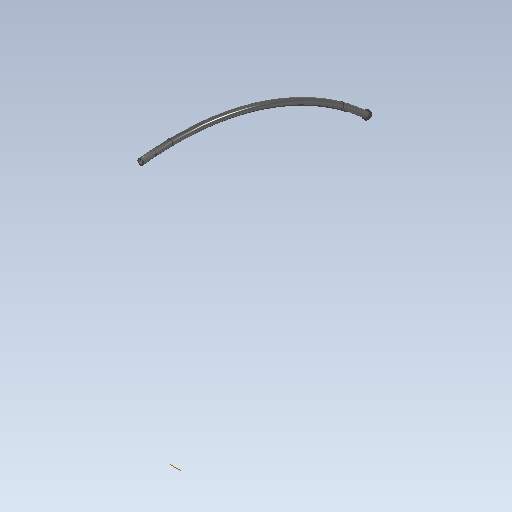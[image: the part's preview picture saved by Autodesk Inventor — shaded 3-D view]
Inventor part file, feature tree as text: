
AUTODESK INVENTOR PART (.ipt)
format: ipt  version: 2021 (Build 250183000, 183)  size: 2,207,744 bytes
history: native  units: mm
features: sketch x10, extrude x8, sweep x2, fillet x2, plane x2, split x2, pattern_circular x1
ambient origin geometry x8: Origin, YZ Plane, XZ Plane, XY Plane, X Axis, Y Axis, Z Axis, Center Point
bodies: Solid1 (feature_tree), Solid2 (feature_tree), Solid3 (feature_tree), Solid6 (feature_tree), Solid7 (feature_tree)
feature tree (27):
  sketch  "Sketch1"  dims[d0=3300.0mm d1=1650.0mm]
  sweep  "Sweep1"
  sweep  "Sweep2"
  extrude  "Extrusion1"  Depth=27.3mm
  extrude  "Extrusion3"  Depth=1650.0mm
  pattern_circular  "Circular Pattern1"  Count=120  [1 undecoded]
  extrude  "Extrusion5"  Depth=1701.0mm
  fillet  "Fillet1"  Radius=200.0mm
  sketch  "Sketch11"  dims[d12=3402.0mm]
  extrude  "Extrusion7"  TaperAngle=0.0deg  [1 undecoded]
  extrude  "Extrusion8"  Depth=10.0mm
  extrude  "Extrusion9"  Depth=10.0mm
  extrude  "Extrusion10"  Depth=0.5mm
  extrude  "Extrusion11"  Depth=1.0mm
  fillet  "Fillet3"  Radius=10.0mm
  plane  "Work Plane2"
  split  "Split1"
  plane  "Work Plane4"
  split  "Split3"
  sketch  "Sketch2"  dims[d2=0.0mm d3=33.7mm]
  sketch  "Sketch3"  dims[d4=0.0mm d5=0.0mm d6=27.3mm]
  sketch  "Sketch4"  dims[d7=0.0mm d8=1650.0mm]
  sketch  "Sketch5"  dims[d9=0.0mm d10=0.0mm]
  sketch  "Sketch9"  dims[d11=1752.0mm]
  sketch  "Sketch12"  dims[d13=1701.0mm d14=1200.0mm]
  sketch  "Sketch13"  dims[d15=1701.0mm d16=1701.0mm d17=200.0mm]
  sketch  "Sketch14"  dims[d18=51.0mm d19=0.0mm d20=19.0mm d21=19.0mm d22=0.5mm d25=1.0mm d26=10.0mm d27=0.0mm d28=680.0mm d29=7.679449mm d38=10.0mm d39=5.0mm d40=10.0mm d41=0.0mm d42=2.0mm d45=2.0mm d46=3300.0mm d47=100.0mm d48=0.0mm d50=10.0mm d51=0.0mm d52=10.0mm d53=12.0mm d54=0.0mm d56=10.0mm d57=0.0mm d58=3300.0mm d59=8.0mm d60=100.0mm d61=0.0mm d62=3.2mm d63=5.0mm d64=2.0mm d65=-200.0mm d67=-170.0mm]
note: 2 required parameter values undecoded (feature->parameter linkage not recoverable at this tier; creation-order binding heuristic only, values carry confidence <= 0.55)
